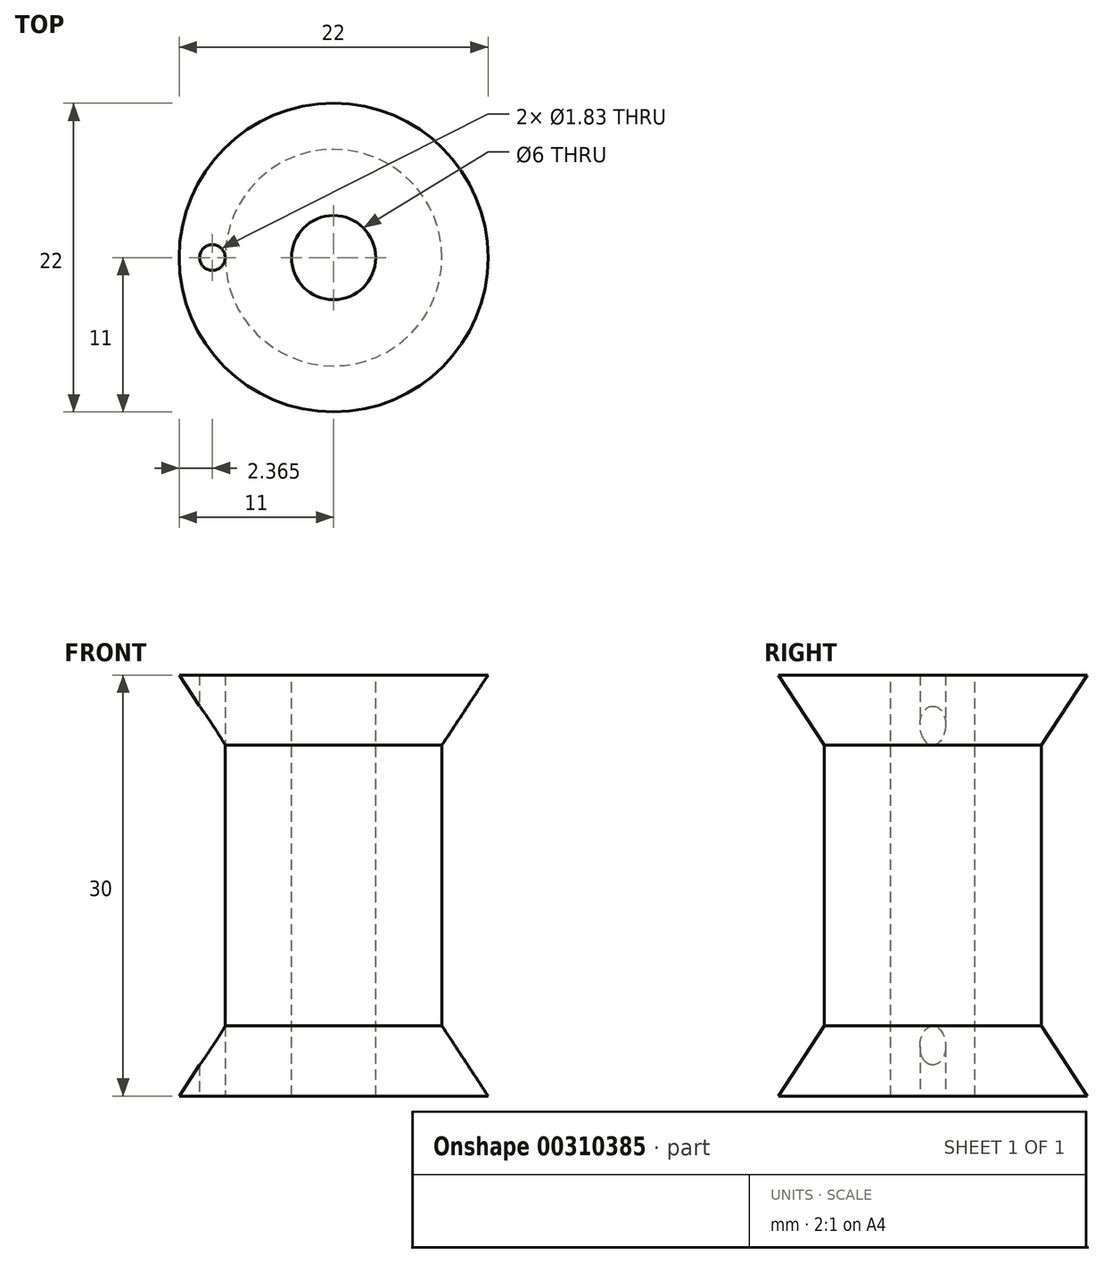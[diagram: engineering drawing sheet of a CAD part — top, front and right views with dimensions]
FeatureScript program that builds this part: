
annotation { "Feature Type Name" : "Feature", "Feature Type Description" : "" }
export const myFeature = defineFeature(function(context is Context, id is Id, definition is map)
    precondition{}
    {
        {
            var Q0;
            Q0=qCreatedBy(makeId("Right.planeOp"),FACE);
            var sketch = newSketch(context, id + "F0", { "sketchPlane" : qUnion([Q0])});
            skLineSegment(sketch, "E0", {"start": v(0, 84.5) * mm, "end": v(0, -101.02) * mm, "construction": true});
            skLineSegment(sketch, "E1", {"start": v(-3, 26.54) * mm, "end": v(-11, 26.54) * mm});
            skLineSegment(sketch, "E2", {"start": v(-11, 26.54) * mm, "end": v(-7.72, 21.54) * mm});
            skLineSegment(sketch, "E3", {"start": v(-7.72, 21.54) * mm, "end": v(-7.72, 1.54) * mm});
            skLineSegment(sketch, "E4", {"start": v(-7.72, 1.54) * mm, "end": v(-11, -3.46) * mm});
            skLineSegment(sketch, "E5", {"start": v(-11, -3.46) * mm, "end": v(-3, -3.46) * mm});
            skLineSegment(sketch, "E6", {"start": v(-3, 26.54) * mm, "end": v(-3, -3.46) * mm});
            skPoint(sketch, "E7.orphan", {"position": v(0, -3.46) * mm});
            skSolve(sketch);
        }
        {
            var Q0;
            Q0=makeQuery(id+"F0.imprint","IMPRINT",FACE,{"disambiguationData":[TD([[makeQuery(id+"F0.imprint","IMPRINT",EDGE,{"derivedFrom":sQuery(id+"F0.wireOp",EDGE,"E1")}),1.0]])]});
            var Q1;
            Q1=sQuery(id+"F0.wireOp",EDGE,"E0");
            revolve(context, id + "F1", {"entities" : qUnion([Q0]), "axis" : qUnion([Q1]), "revolveType" : RevolveType.FULL});
        }
        {
            var Q0;
            Q0=makeQuery(id+"F1.opRevolve","SWEPT_FACE",FACE,{"disambiguationData":[OSD([sQuery(id+"F0.wireOp",EDGE,"E5")])]});
            var sketch = newSketch(context, id + "F2", { "sketchPlane" : qUnion([Q0])});
            skCircle(sketch, "E8", {"center": v(-8.64, 0) * mm, "radius": 0.91 * mm});
            skSolve(sketch);
        }
        {
            var Q0;
            Q0 = qSketchRegion(id + "F2", true);
            extrude(context, id + "F3", {"entities" : qUnion([Q0]), "operationType" : NewBodyOperationType.REMOVE, "oppositeDirection" : true, "depth" : 30 * mm});
        }
    });
